# Revit family: 4069478 Sylvania Lighting Fixture PATHE GROUND DECO MONO3 ELLIPTICAL 320LM LED 4K
name_source: partatom
category: Lighting Fixtures
revit_build: Autodesk Revit 2016 (Build: 20150220_1215(x64)
units: mm (PartAtom-declared; Revit-internal decimal feet)

## family parameters
Cut with Voids When Loaded = No
Host = Face
Light Source = No
OmniClass Number = 23.80.70.00
OmniClass Title = Lighting
Part Type = Normal
Room Calculation Point = No
Round Connector Dimension = Use Diameter
Shared = No

## types (1)
- 4069478 PATHE/G/DM3 ELLIP 320LM LED 4K
    AngleOpeningMINUS_SYL = -55.00°
    AngleOpening_SYL = 55.00°
    Apparent Load = 11 VA
    Assembly Code = D5020200
    AssetType = Fixed
    ClassificationName = Uniclass2015
    ClassificationValue = EF_70_80
    Cost = 0 $
    Default Elevation = 1219 mm
    Description = Single emission recessed ground luminaire, Corrosion resistant die-cast aluminium, 320lm, 11W, 29lm/W, 4000K, CRI80+, 13°,40°, non dimmable, IP67, IK10, (ØxD) Ø215x245mm, 3, Class I, 220-240V, A++ A+ A
    DocumentationLiterature = http://www.sylvania-lighting.com
    DurationUnit = hours
    ElectricShockClassification = Class I
    EmittionSurface_SYL = 64 mm
    ExpectedLife = 50000
    HeightDome_SYL = 45 mm  [stored 0.147638 ft]
    HieghtGround_SYL = 200 mm  [stored 0.656168 ft]
    IfcExportAs = IfcLightFixtureType
    IfcExportType = IfcLightFixtureType
    ImpactProtectionIndex = IK10
    IngressProtection = IP67
    Keynote = 16500
    Lamp = LED
    LampColourRenderingIndex = 80
    LampColourTemperature = 4000 K
    LampNominalLuminous = 320 lm
    LampsType = LED
    LightOutputRatio = 100
    LuminousEfficacy = 29.09 lm/W
    Manufacturer = Feilo Sylvania
    ManufacturerName = Feilo Sylvania
    Material = corrosion resistant die-cast aluminium housing, uv-resistant polycarbonate diffuser
    Material_1_SYL = Aluminum 6061 T6 80 Hot Formed
    Material_2_SYL = PC-Sylvania-PatheDM-Glow
    Material_3_SYL = <By Category>
    Material_4_SYL = <By Category>
    Model = PATHE/GROUND/DECO MONO3 ELLIPTICAL 320LM LED 4K
    ModelNumber = 4069478
    ModelReference = PATHE/GROUND/DECO MONO3 ELLIPTICAL 320LM LED 4K
    Name = PATHE/GROUND/DECO MONO3 ELLIPTICAL 320LM LED 4K
    NominalDepth = 0 mm  [stored 0 ft]
    NominalHeight = 200 mm  [stored 0.656168 ft]
    NominalLength = 215 mm
    Offset_SYL = 0 mm  [stored 0 ft]
    PowerConsumption = 11 W
    PowerFactor = 0
    RadiusDiffuserBottom_SYL = 70 mm  [stored 0.229659 ft]
    RadiusDome_SYL = 169 mm
    RadiusOpeningTop_SYL = 50 mm  [stored 0.164042 ft]
    RadiusRef_SYL = 120 mm  [stored 0.393701 ft]
    Radius_SYL = 108 mm  [stored 0.354331 ft]
    Type Image = <None>
    TypeLight_SYL = Pathe DM light : 4069478 PATHE/G/DM3 ELLIP 320LM LED 4K
    TypeName = PATHE/GROUND/DECO MONO3 ELLIPTICAL 320LM LED 4K
    URL = http://www.sylvania-lighting.com
    Voltage = 0 V
    Weight = 3.3 kg

note: [stored X ft] marks values corroborated as IEEE doubles in the binary element streams (Revit-internal decimal feet)

## geometry (parser evidence)
native form markers: Sweep x6
no freeform markers — native parametric forms only
